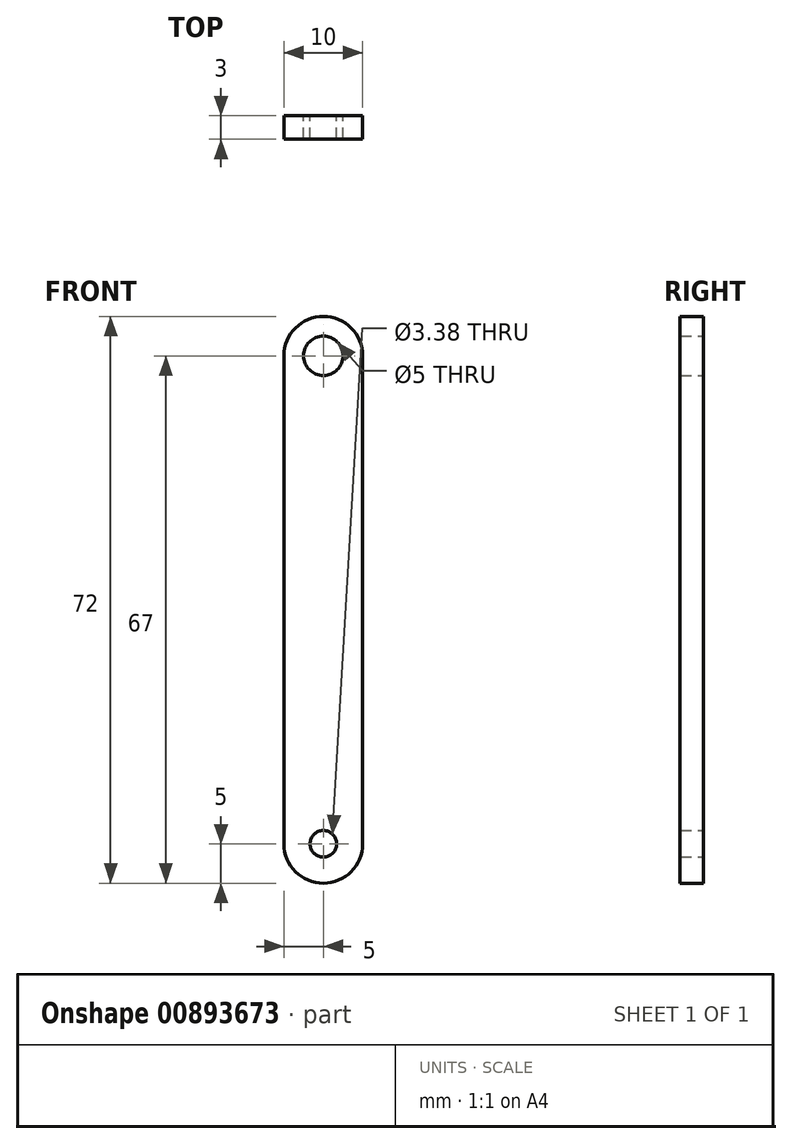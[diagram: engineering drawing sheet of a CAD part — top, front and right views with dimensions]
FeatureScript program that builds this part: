
annotation { "Feature Type Name" : "Feature", "Feature Type Description" : "" }
export const myFeature = defineFeature(function(context is Context, id is Id, definition is map)
    precondition{}
    {
        {
            var Q0;
            Q0=qCreatedBy(makeId("Front.planeOp"),FACE);
            var sketch = newSketch(context, id + "F0", { "sketchPlane" : qUnion([Q0])});
            skLineSegment(sketch, "E0.left", {"start": v(5, -31) * mm, "end": v(5, 31) * mm});
            skLineSegment(sketch, "E0.right", {"start": v(-5, -31) * mm, "end": v(-5, 31) * mm});
            skPoint(sketch, "E0.middle", {"position": v(0, 0) * mm});
            skArc(sketch, "E1", {"start": v(5, 31) * mm, "mid": v(0, 36) * mm, "end": v(-5, 31) * mm});
            skArc(sketch, "E2", {"start": v(-5, -31) * mm, "mid": v(0, -36) * mm, "end": v(5, -31) * mm});
            skCircle(sketch, "E3", {"center": v(0, -31) * mm, "radius": 1.69 * mm});
            skCircle(sketch, "E4", {"center": v(0, 31) * mm, "radius": 2.5 * mm});
            skSolve(sketch);
        }
        {
            var Q0;
            Q0=qSketchRegion(id+"F0",true);
            extrude(context, id + "F1", {"entities" : qUnion([Q0]), "depth" : 3 * mm, "offsetDistance" : 25 * mm});
        }
    });
